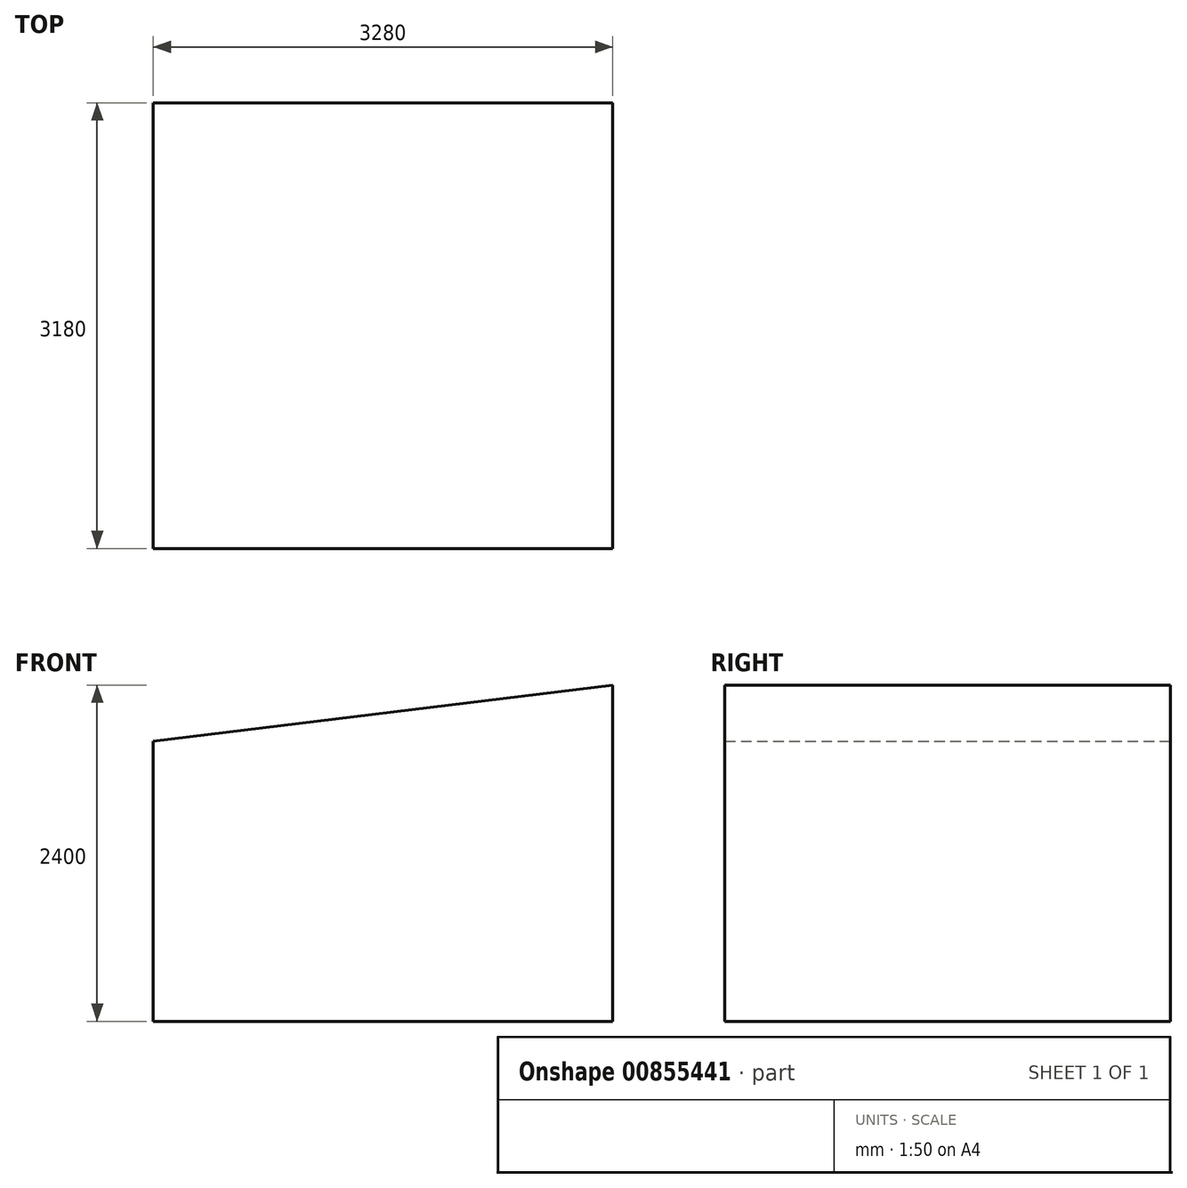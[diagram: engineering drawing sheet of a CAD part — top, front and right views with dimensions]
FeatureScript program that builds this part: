
annotation { "Feature Type Name" : "Feature", "Feature Type Description" : "" }
export const myFeature = defineFeature(function(context is Context, id is Id, definition is map)
    precondition{}
    {
        {
            var Q0;
            Q0=qCreatedBy(makeId("Front.planeOp"),FACE);
            var sketch = newSketch(context, id + "F0", { "sketchPlane" : qUnion([Q0])});
            skLineSegment(sketch, "E0", {"start": v(-1612.55, 0) * mm, "end": v(1667.45, 0) * mm});
            skLineSegment(sketch, "E1", {"start": v(1667.45, 0) * mm, "end": v(1667.45, 2400) * mm});
            skLineSegment(sketch, "E2", {"start": v(-1612.55, 0) * mm, "end": v(-1612.55, 2000) * mm});
            skLineSegment(sketch, "E3", {"start": v(-1612.55, 2000) * mm, "end": v(1667.45, 2400) * mm});
            skSolve(sketch);
        }
        {
            var Q0;
            Q0 = qSketchRegion(id + "F0", true);
            extrude(context, id + "F1", {"entities" : qUnion([Q0]), "depth" : 3180 * mm, "offsetDistance" : 25 * mm});
        }
    });
